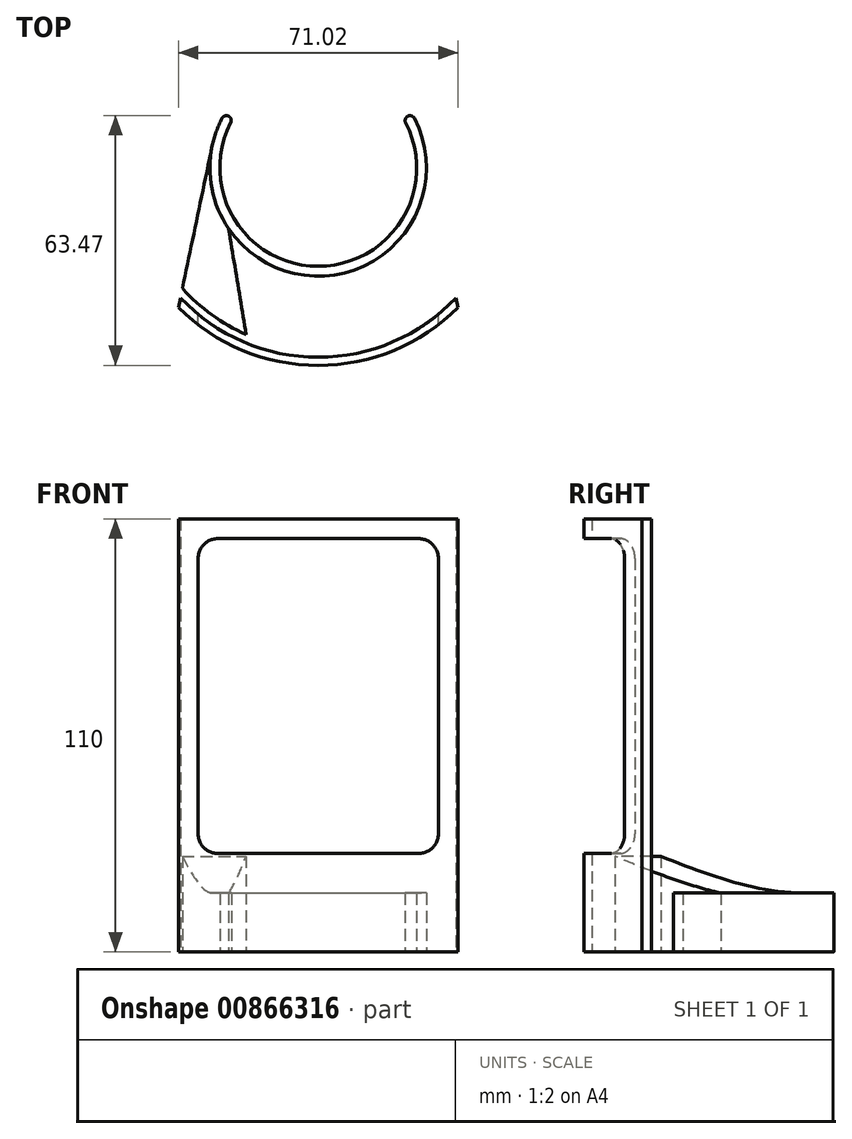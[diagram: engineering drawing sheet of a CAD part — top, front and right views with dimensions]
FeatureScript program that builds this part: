
annotation { "Feature Type Name" : "Feature", "Feature Type Description" : "" }
export const myFeature = defineFeature(function(context is Context, id is Id, definition is map)
    precondition{}
    {
        {
            var Q0;
            Q0=qCreatedBy(makeId("Top.planeOp"),FACE);
            var sketch = newSketch(context, id + "F0", { "sketchPlane" : qUnion([Q0])});
            skCircle(sketch, "E0", {"center": v(0, 0) * mm, "radius": 25 * mm});
            skCircle(sketch, "E1", {"center": v(0, 0) * mm, "radius": 27.5 * mm});
            skLineSegment(sketch, "E2", {"start": v(-26.92, 5.63) * mm, "end": v(-35.51, -35.47) * mm});
            skArc(sketch, "E3", {"start": v(-35.51, -35.47) * mm, "mid": v(0, -50.19) * mm, "end": v(35.51, -35.47) * mm});
            skArc(sketch, "E4", {"start": v(35, -33.02) * mm, "mid": v(0, -48.12) * mm, "end": v(-35, -33.02) * mm});
            skArc(sketch, "E5", {"start": v(-34.49, -30.57) * mm, "mid": v(0, -46.09) * mm, "end": v(34.49, -30.57) * mm});
            skPoint(sketch, "E5.startSnap0", {"position": v(0, -50.19) * mm});
            skLineSegment(sketch, "E6", {"start": v(-18.3, -42.3) * mm, "end": v(-24.66, -4.11) * mm});
            skLineSegment(sketch, "E7", {"start": v(35.51, -35.47) * mm, "end": v(35, -33.02) * mm});
            skLineSegment(sketch, "E8", {"start": v(34.49, -30.57) * mm, "end": v(35, -33.02) * mm});
            skLineSegment(sketch, "E9", {"start": v(-26.92, 5.63) * mm, "end": v(-24.66, -4.11) * mm});
            skLineSegment(sketch, "E10", {"start": v(-21.65, 12.5) * mm, "end": v(-23.82, 13.75) * mm});
            skLineSegment(sketch, "E11", {"start": v(21.65, 12.5) * mm, "end": v(23.82, 13.75) * mm});
            skSolve(sketch);
        }
        {
            var Q0;
            {var subQ0=sQuery(id+"F0.wireOp",EDGE,"E9");Q0=makeQuery(id+"F0.imprint","IMPRINT",FACE,{"disambiguationData":[TD([[makeQuery(id+"F0.imprint","IMPRINT",EDGE,{"derivedFrom":subQ0}),1.0]])]});}
            var Q1;
            {var subQ3=sQuery(id+"F0.wireOp",EDGE,"E11");Q1=makeQuery(id+"F0.imprint","IMPRINT",FACE,{"disambiguationData":[TD([[makeQuery(id+"F0.imprint","IMPRINT",EDGE,{"derivedFrom":subQ3}),-1.0]])]});}
            var Q2;
            {var subQ0=sQuery(id+"F0.wireOp",EDGE,"E9");Q2=makeQuery(id+"F0.imprint","IMPRINT",FACE,{"disambiguationData":[TD([[makeQuery(id+"F0.imprint","IMPRINT",EDGE,{"derivedFrom":subQ0}),-1.0]])]});}
            extrude(context, id + "F1", {"entities" : qUnion([Q0, Q1, Q2]), "depth" : 15 * mm, "offsetDistance" : 25 * mm});
        }
        {
            var Q0;
            {var subQ0=sQuery(id+"F0.wireOp",EDGE,"E2");var subQ5=sQuery(id+"F0.wireOp",EDGE,"E5");var subQ6=makeQuery(id+"F0.imprint","INTERSECT",VERTEX,{"derivedFrom":[subQ0,subQ5]});Q0=makeQuery(id+"F0.imprint","IMPRINT",FACE,{"disambiguationData":[TD([[makeQuery(id+"F0.imprint","IMPRINT",EDGE,{"disambiguationData":[TD([[subQ6,-1.0]])],"derivedFrom":subQ5}),1.0]])]});}
            extrude(context, id + "F2", {"entities" : qUnion([Q0]), "operationType" : NewBodyOperationType.ADD, "depth" : 25 * mm, "offsetDistance" : 25 * mm});
        }
        {
            var Q0;
            Q0=makeQuery(id+"F2.opExtrude","CAP_EDGE",EDGE,{"disambiguationData":[OSD([sQuery(id+"F0.wireOp",EDGE,"E1")])],"isStart":false});
            chamfer(context, id + "F3", {"entities" : qUnion([Q0]), "chamferType" : ChamferType.TWO_OFFSETS, "width1" : 10 * mm, "oppositeDirection" : false, "width2" : 20 * mm, "tangentPropagation" : true});
        }
        {
            var Q0;
            {var subQ4=sQuery(id+"F0.wireOp",EDGE,"E4");Q0=makeQuery(id+"F0.imprint","IMPRINT",FACE,{"disambiguationData":[TD([[makeQuery(id+"F0.imprint","IMPRINT",EDGE,{"derivedFrom":subQ4}),-1.0]])]});}
            extrude(context, id + "F4", {"entities" : qUnion([Q0]), "operationType" : NewBodyOperationType.ADD, "depth" : 110 * mm, "offsetDistance" : 25 * mm});
        }
        {
            var Q0;
            {var subQ0=sQuery(id+"F0.wireOp",EDGE,"E3");Q0=makeQuery(id+"F0.imprint","IMPRINT",FACE,{"disambiguationData":[TD([[makeQuery(id+"F0.imprint","IMPRINT",EDGE,{"derivedFrom":subQ0}),1.0]])]});}
            extrude(context, id + "F5", {"entities" : qUnion([Q0]), "depth" : 110 * mm, "offsetDistance" : 25 * mm});
        }
        {
            var Q0;
            Q0=makeQuery(id+"F1.opExtrude","SWEPT_EDGE",EDGE,{"disambiguationData":[OSD([sQuery(id+"F0.wireOp",EDGE,"E1"),sQuery(id+"F0.wireOp",EDGE,"E10")])]});
            var Q1;
            Q1=makeQuery(id+"F1.opExtrude","SWEPT_EDGE",EDGE,{"disambiguationData":[OSD([sQuery(id+"F0.wireOp",EDGE,"E0"),sQuery(id+"F0.wireOp",EDGE,"E10")])]});
            var Q2;
            Q2=makeQuery(id+"F1.opExtrude","SWEPT_EDGE",EDGE,{"disambiguationData":[OSD([sQuery(id+"F0.wireOp",EDGE,"E1"),sQuery(id+"F0.wireOp",EDGE,"E11")])]});
            var Q3;
            Q3=makeQuery(id+"F1.opExtrude","SWEPT_EDGE",EDGE,{"disambiguationData":[OSD([sQuery(id+"F0.wireOp",EDGE,"E0"),sQuery(id+"F0.wireOp",EDGE,"E11")])]});
            fillet(context, id + "F6", {"entities" : qUnion([Q0, Q1, Q2, Q3]), "radius" : 1.25 * mm, "tangentPropagation" : true, "allowEdgeOverflow" : false});
        }
        {
            var Q0;
            Q0=qCreatedBy(makeId("Front.planeOp"),FACE);
            var sketch = newSketch(context, id + "F7", { "sketchPlane" : qUnion([Q0])});
            skLineSegment(sketch, "E12.0", {"start": v(-35.51, 110) * mm, "end": v(35.51, 110) * mm});
            skLineSegment(sketch, "E13.0", {"start": v(-35.51, 110) * mm, "end": v(-35.51, 0) * mm});
            skLineSegment(sketch, "E14.0", {"start": v(35.51, 110) * mm, "end": v(35.51, 0) * mm});
            skLineSegment(sketch, "E15.bottom", {"start": v(-30.51, 105) * mm, "end": v(30.51, 105) * mm});
            skLineSegment(sketch, "E15.top", {"start": v(-30.51, 25) * mm, "end": v(30.51, 25) * mm});
            skLineSegment(sketch, "E15.left", {"start": v(-30.51, 105) * mm, "end": v(-30.51, 25) * mm});
            skLineSegment(sketch, "E15.right", {"start": v(30.51, 105) * mm, "end": v(30.51, 25) * mm});
            skSolve(sketch);
        }
        {
            var Q0;
            Q0=makeQuery(id+"F7.imprint","IMPRINT",FACE,{"disambiguationData":[TD([[makeQuery(id+"F7.imprint","IMPRINT",EDGE,{"derivedFrom":sQuery(id+"F7.wireOp",EDGE,"E15.bottom")}),-1.0]])]});
            extrude(context, id + "F8", {"entities" : qUnion([Q0]), "operationType" : NewBodyOperationType.REMOVE, "depth" : 76.7 * mm, "offsetDistance" : 25 * mm});
        }
        {
            var Q0;
            {var subQ0=sQuery(id+"F7.wireOp",EDGE,"E15.right");var subQ1=sQuery(id+"F7.wireOp",EDGE,"E15.top");Q0=makeQuery(id+"F8.boolean.opBoolean","COPY",EDGE,{"disambiguationData":[TD([makeQuery(id+"F5.opExtrude","SWEPT_FACE",FACE,{"disambiguationData":[OSD([sQuery(id+"F0.wireOp",EDGE,"E3")])]})])],"derivedFrom":makeQuery(id+"F8.opExtrude","SWEPT_EDGE",EDGE,{"disambiguationData":[OSD([subQ1,subQ0])]})});}
            var Q1;
            {var subQ0=sQuery(id+"F7.wireOp",EDGE,"E15.bottom");var subQ1=sQuery(id+"F7.wireOp",EDGE,"E15.right");Q1=makeQuery(id+"F8.boolean.opBoolean","COPY",EDGE,{"disambiguationData":[TD([makeQuery(id+"F5.opExtrude","SWEPT_FACE",FACE,{"disambiguationData":[OSD([sQuery(id+"F0.wireOp",EDGE,"E3")])]})])],"derivedFrom":makeQuery(id+"F8.opExtrude","SWEPT_EDGE",EDGE,{"disambiguationData":[OSD([subQ0,subQ1])]})});}
            var Q2;
            {var subQ0=sQuery(id+"F7.wireOp",EDGE,"E15.top");var subQ1=sQuery(id+"F7.wireOp",EDGE,"E15.left");Q2=makeQuery(id+"F8.boolean.opBoolean","COPY",EDGE,{"disambiguationData":[TD([makeQuery(id+"F4.opExtrude","SWEPT_FACE",FACE,{"disambiguationData":[OSD([sQuery(id+"F0.wireOp",EDGE,"E4")])]})])],"derivedFrom":makeQuery(id+"F8.opExtrude","SWEPT_EDGE",EDGE,{"disambiguationData":[OSD([subQ0,subQ1])]})});}
            var Q3;
            {var subQ0=sQuery(id+"F7.wireOp",EDGE,"E15.left");var subQ1=sQuery(id+"F7.wireOp",EDGE,"E15.top");Q3=makeQuery(id+"F8.boolean.opBoolean","COPY",EDGE,{"disambiguationData":[TD([makeQuery(id+"F5.opExtrude","SWEPT_FACE",FACE,{"disambiguationData":[OSD([sQuery(id+"F0.wireOp",EDGE,"E3")])]})])],"derivedFrom":makeQuery(id+"F8.opExtrude","SWEPT_EDGE",EDGE,{"disambiguationData":[OSD([subQ1,subQ0])]})});}
            var Q4;
            {var subQ0=sQuery(id+"F7.wireOp",EDGE,"E15.bottom");var subQ1=sQuery(id+"F7.wireOp",EDGE,"E15.left");Q4=makeQuery(id+"F8.boolean.opBoolean","COPY",EDGE,{"disambiguationData":[TD([makeQuery(id+"F4.opExtrude","SWEPT_FACE",FACE,{"disambiguationData":[OSD([sQuery(id+"F0.wireOp",EDGE,"E4")])]})])],"derivedFrom":makeQuery(id+"F8.opExtrude","SWEPT_EDGE",EDGE,{"disambiguationData":[OSD([subQ0,subQ1])]})});}
            var Q5;
            {var subQ0=sQuery(id+"F7.wireOp",EDGE,"E15.left");var subQ1=sQuery(id+"F7.wireOp",EDGE,"E15.bottom");Q5=makeQuery(id+"F8.boolean.opBoolean","COPY",EDGE,{"disambiguationData":[TD([makeQuery(id+"F5.opExtrude","SWEPT_FACE",FACE,{"disambiguationData":[OSD([sQuery(id+"F0.wireOp",EDGE,"E3")])]})])],"derivedFrom":makeQuery(id+"F8.opExtrude","SWEPT_EDGE",EDGE,{"disambiguationData":[OSD([subQ1,subQ0])]})});}
            var Q6;
            {var subQ0=sQuery(id+"F7.wireOp",EDGE,"E15.top");var subQ1=sQuery(id+"F7.wireOp",EDGE,"E15.right");Q6=makeQuery(id+"F8.boolean.opBoolean","COPY",EDGE,{"disambiguationData":[TD([makeQuery(id+"F4.opExtrude","SWEPT_FACE",FACE,{"disambiguationData":[OSD([sQuery(id+"F0.wireOp",EDGE,"E4")])]})])],"derivedFrom":makeQuery(id+"F8.opExtrude","SWEPT_EDGE",EDGE,{"disambiguationData":[OSD([subQ0,subQ1])]})});}
            var Q7;
            {var subQ0=sQuery(id+"F7.wireOp",EDGE,"E15.bottom");var subQ1=sQuery(id+"F7.wireOp",EDGE,"E15.right");Q7=makeQuery(id+"F8.boolean.opBoolean","COPY",EDGE,{"disambiguationData":[TD([makeQuery(id+"F4.opExtrude","SWEPT_FACE",FACE,{"disambiguationData":[OSD([sQuery(id+"F0.wireOp",EDGE,"E4")])]})])],"derivedFrom":makeQuery(id+"F8.opExtrude","SWEPT_EDGE",EDGE,{"disambiguationData":[OSD([subQ0,subQ1])]})});}
            fillet(context, id + "F9", {"entities" : qUnion([Q0, Q1, Q2, Q3, Q4, Q5, Q6, Q7]), "radius" : 5 * mm, "tangentPropagation" : true, "allowEdgeOverflow" : false});
        }
    });
